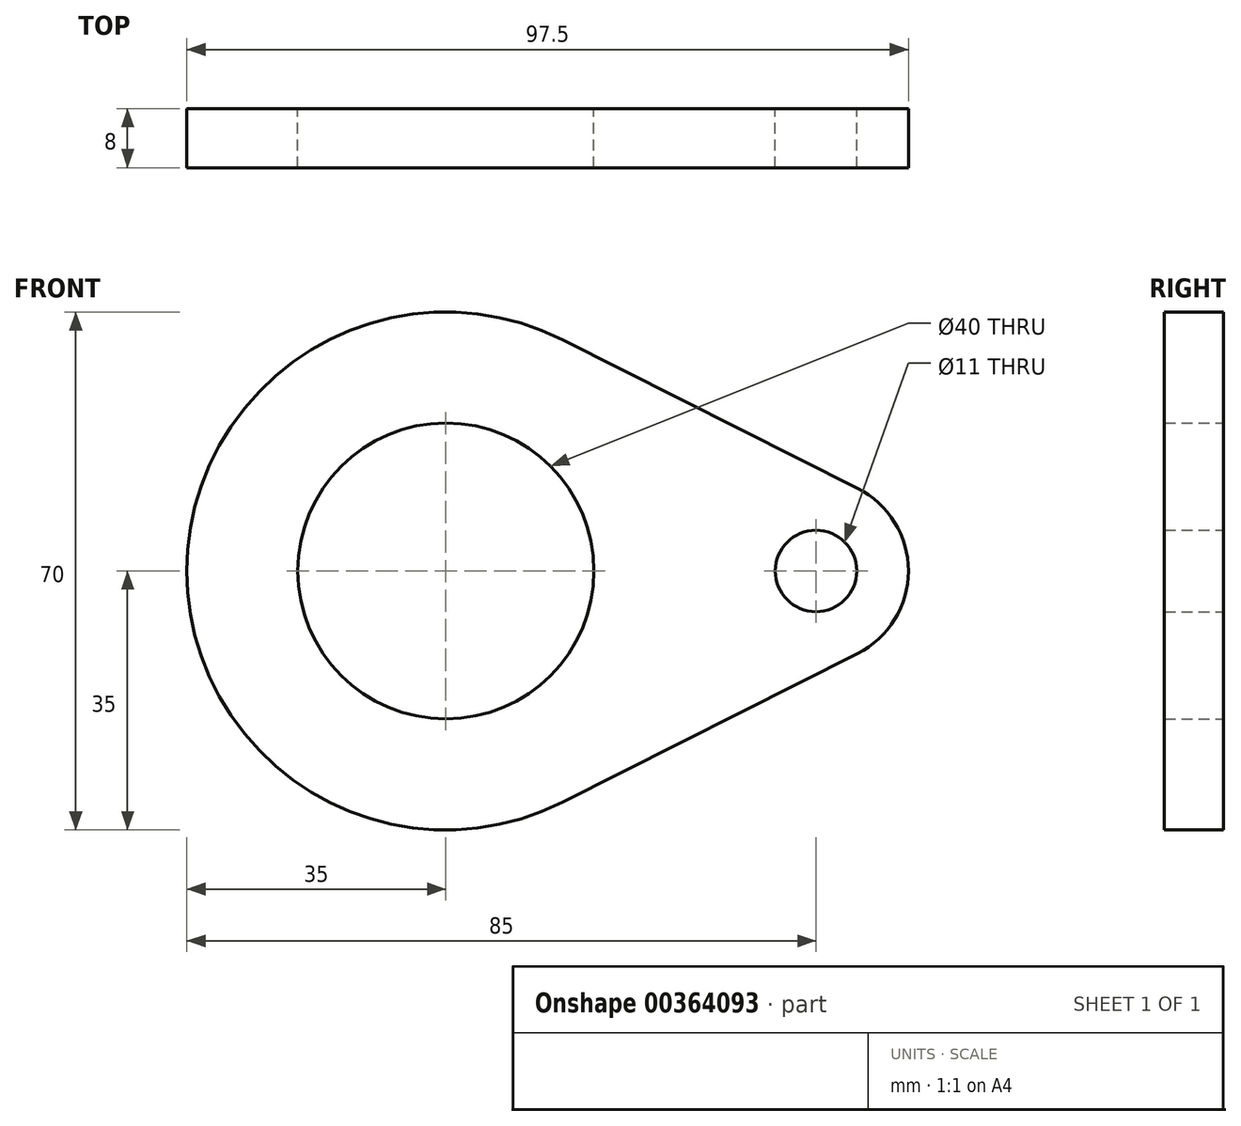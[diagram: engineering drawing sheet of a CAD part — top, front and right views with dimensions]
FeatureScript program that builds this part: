
annotation { "Feature Type Name" : "Feature", "Feature Type Description" : "" }
export const myFeature = defineFeature(function(context is Context, id is Id, definition is map)
    precondition{}
    {
        {
            var Q0;
            Q0=qCreatedBy(makeId("Front.planeOp"),FACE);
            var sketch = newSketch(context, id + "F0", { "sketchPlane" : qUnion([Q0])});
            skCircle(sketch, "E0", {"center": v(0, 0) * mm, "radius": 20 * mm});
            skArc(sketch, "E1", {"start": v(15.75, 31.26) * mm, "mid": v(-35, 0) * mm, "end": v(15.75, -31.26) * mm});
            skCircle(sketch, "E2", {"center": v(50, 0) * mm, "radius": 5.5 * mm});
            skArc(sketch, "E3", {"start": v(55.62, -11.16) * mm, "mid": v(62.5, 0) * mm, "end": v(55.62, 11.16) * mm});
            skLineSegment(sketch, "E4", {"start": v(55.62, -11.16) * mm, "end": v(15.75, -31.26) * mm});
            skLineSegment(sketch, "E5", {"start": v(15.75, 31.26) * mm, "end": v(55.63, 11.16) * mm});
            skPoint(sketch, "E6", {"position": v(55.62, 11.16) * mm});
            skPoint(sketch, "E7", {"position": v(55.62, -11.16) * mm});
            skSolve(sketch);
        }
        {
            var Q0;
            Q0=makeQuery(id+"F0.imprint","IMPRINT",FACE,{"disambiguationData":[TD([[makeQuery(id+"F0.imprint","IMPRINT",EDGE,{"derivedFrom":sQuery(id+"F0.wireOp",EDGE,"E0")}),-1.0]])]});
            extrude(context, id + "F1", {"entities" : qUnion([Q0]), "depth" : 8 * mm});
        }
    });
